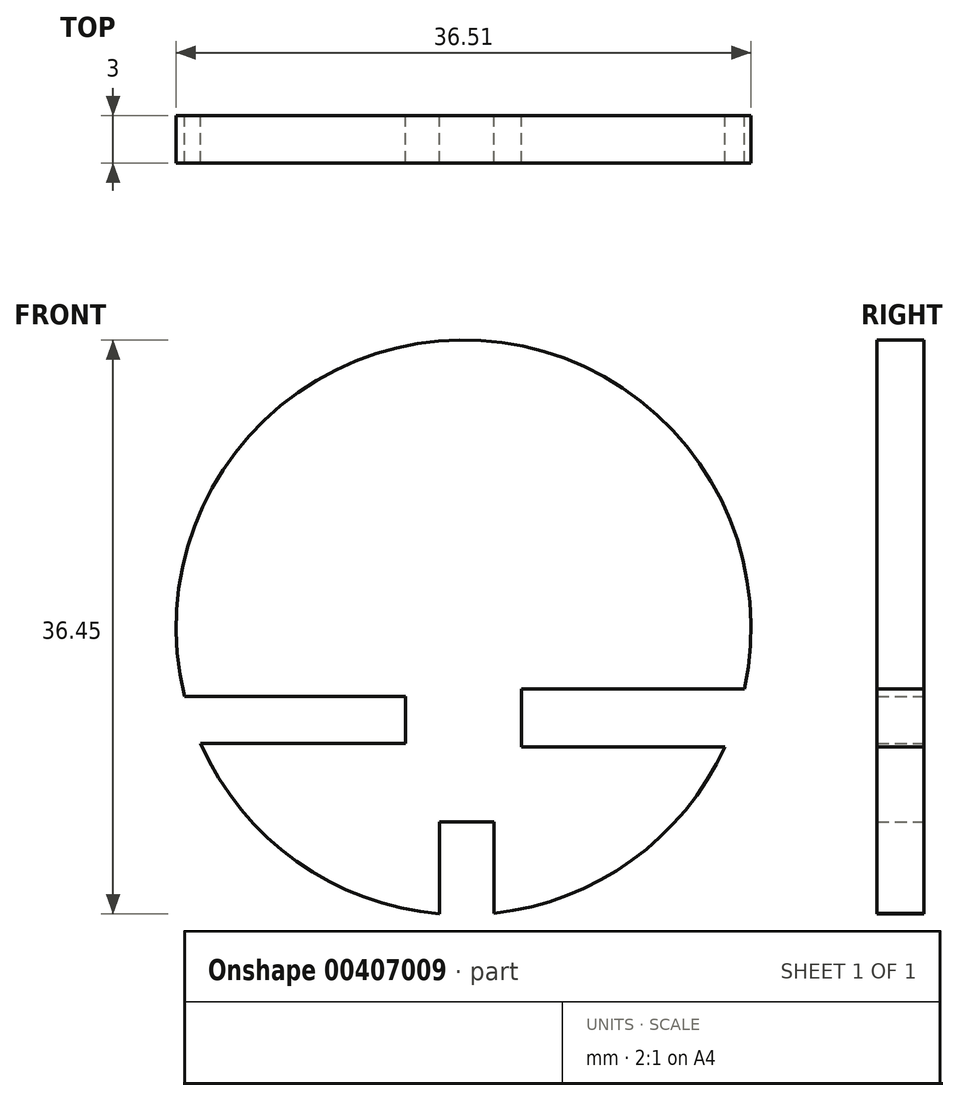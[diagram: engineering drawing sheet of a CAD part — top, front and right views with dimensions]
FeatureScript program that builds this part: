
annotation { "Feature Type Name" : "Feature", "Feature Type Description" : "" }
export const myFeature = defineFeature(function(context is Context, id is Id, definition is map)
    precondition{}
    {
        {
            var Q0;
            Q0=qCreatedBy(makeId("Front.planeOp"),FACE);
            var sketch = newSketch(context, id + "F0", { "sketchPlane" : qUnion([Q0])});
            skArc(sketch, "E0", {"start": v(-17.6, -8.64) * mm, "mid": v(0, -19.95) * mm, "end": v(17.6, -8.64) * mm});
            skLineSegment(sketch, "E1.bottom", {"start": v(-18.6, -5.92) * mm, "end": v(-1.32, -5.92) * mm});
            skLineSegment(sketch, "E1.top", {"start": v(-17.6, -8.64) * mm, "end": v(-1.32, -8.64) * mm});
            skLineSegment(sketch, "E2.left", {"start": v(-1.32, -5.92) * mm, "end": v(-1.32, -8.64) * mm});
            skLineSegment(sketch, "E2.right", {"start": v(1.1, -5.92) * mm, "end": v(1.1, -8.64) * mm});
            skLineSegment(sketch, "E3.trimOffspring", {"start": v(1.1, -5.92) * mm, "end": v(18.6, -5.92) * mm});
            skLineSegment(sketch, "E4.trimOffspring", {"start": v(1.1, -8.64) * mm, "end": v(17.6, -8.64) * mm});
            skArc(sketch, "E5.trimOffspring", {"start": v(18.6, -5.92) * mm, "mid": v(0, 18.73) * mm, "end": v(-18.6, -5.92) * mm});
            skSolve(sketch);
        }
        {
            var Q0;
            Q0=makeQuery(id+"F0.imprint","IMPRINT",FACE,{"disambiguationData":[TD([[makeQuery(id+"F0.imprint","IMPRINT",EDGE,{"derivedFrom":sQuery(id+"F0.wireOp",EDGE,"E0")}),1.0]])]});
            var sketch = newSketch(context, id + "F1", { "sketchPlane" : qUnion([Q0])});
            skLineSegment(sketch, "E6", {"start": v(-18.54, -5.92) * mm, "end": v(-17.77, -8.45) * mm});
            skLineSegment(sketch, "E7", {"start": v(17.46, -9) * mm, "end": v(18.78, -6.25) * mm});
            skSolve(sketch);
        }
        {
            var Q0;
            Q0=makeQuery(id+"F1.imprint","IMPRINT",FACE,{"disambiguationData":[TD([[makeQuery(id+"F1.imprint","IMPRINT",EDGE,{"derivedFrom":makeQuery(id+"F0.imprint","IMPRINT",EDGE,{"derivedFrom":sQuery(id+"F0.wireOp",EDGE,"E0")})}),1.0]])]});
            extrude(context, id + "F2", {"entities" : qUnion([Q0]), "depth" : 3 * mm});
        }
        {
            var Q0;
            Q0=makeQuery(id+"F2.opExtrude","CAP_FACE",FACE,{"disambiguationData":[OSD([sQuery(id+"F0.wireOp",EDGE,"E0"),sQuery(id+"F0.wireOp",EDGE,"E1.bottom"),sQuery(id+"F0.wireOp",EDGE,"E1.top"),sQuery(id+"F0.wireOp",EDGE,"E2.left"),sQuery(id+"F0.wireOp",EDGE,"E2.right"),sQuery(id+"F0.wireOp",EDGE,"E3.trimOffspring"),sQuery(id+"F0.wireOp",EDGE,"E4.trimOffspring"),sQuery(id+"F0.wireOp",EDGE,"E5.trimOffspring")])],"isStart":false});
            var sketch = newSketch(context, id + "F3", { "sketchPlane" : qUnion([Q0])});
            skLineSegment(sketch, "E8.bottom", {"start": v(-1.33, -13.6) * mm, "end": v(1.58, -13.6) * mm});
            skLineSegment(sketch, "E8.left", {"start": v(-1.33, -13.6) * mm, "end": v(-1.33, -19.9) * mm});
            skLineSegment(sketch, "E8.right", {"start": v(1.58, -13.6) * mm, "end": v(1.58, -19.95) * mm});
            skPoint(sketch, "E9.endSnap0", {"position": v(0, -19.95) * mm});
            skArc(sketch, "E10", {"start": v(-67.26, 45.94) * mm, "mid": v(-61.15, 38.44) * mm, "end": v(-52.07, 35.11) * mm});
            skLineSegment(sketch, "E11.bottom", {"start": v(-68.28, 48.93) * mm, "end": v(-54.23, 48.93) * mm});
            skLineSegment(sketch, "E11.top", {"start": v(-68.28, 45.94) * mm, "end": v(-54.23, 45.94) * mm});
            skLineSegment(sketch, "E11.right", {"start": v(-54.23, 48.93) * mm, "end": v(-54.23, 45.94) * mm});
            skLineSegment(sketch, "E12.bottom", {"start": v(-46.87, 49.4) * mm, "end": v(-32.72, 49.4) * mm});
            skLineSegment(sketch, "E12.top", {"start": v(-46.87, 45.73) * mm, "end": v(-33.95, 45.73) * mm});
            skLineSegment(sketch, "E12.left", {"start": v(-46.87, 49.4) * mm, "end": v(-46.87, 45.73) * mm});
            skLineSegment(sketch, "E13.bottom", {"start": v(-52.07, 40.96) * mm, "end": v(-48.6, 40.96) * mm});
            skLineSegment(sketch, "E13.left", {"start": v(-52.07, 40.96) * mm, "end": v(-52.07, 35.11) * mm});
            skLineSegment(sketch, "E13.right", {"start": v(-48.6, 40.96) * mm, "end": v(-48.6, 35.15) * mm});
            skArc(sketch, "E14.trimOffspring", {"start": v(-48.6, 35.15) * mm, "mid": v(-39.87, 38.5) * mm, "end": v(-33.95, 45.73) * mm});
            skArc(sketch, "E15.trimOffspring", {"start": v(-32.72, 49.4) * mm, "mid": v(-50.8, 71.56) * mm, "end": v(-68.28, 48.93) * mm});
            skSolve(sketch);
        }
        {
            var Q0;
            Q0 = qSketchRegion(id + "F3", true);
            extrude(context, id + "F4", {"entities" : qUnion([Q0]), "depth" : 3 * mm});
        }
        {
            var Q0;
            Q0=makeQuery(id+"F2.opExtrude","SWEPT_BODY",BODY,{"disambiguationData":[OSD([sQuery(id+"F0.wireOp",EDGE,"E0"),sQuery(id+"F0.wireOp",EDGE,"E1.bottom"),sQuery(id+"F0.wireOp",EDGE,"E1.top"),sQuery(id+"F0.wireOp",EDGE,"E2.left"),sQuery(id+"F0.wireOp",EDGE,"E2.right"),sQuery(id+"F0.wireOp",EDGE,"E3.trimOffspring"),sQuery(id+"F0.wireOp",EDGE,"E4.trimOffspring"),sQuery(id+"F0.wireOp",EDGE,"E5.trimOffspring")])]});
            deleteBodies(context, id + "F5", {"entities" : qUnion([Q0])});
        }
    });
